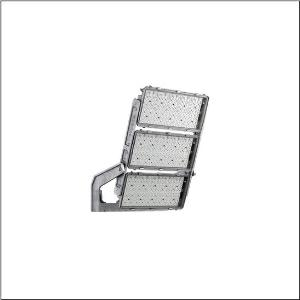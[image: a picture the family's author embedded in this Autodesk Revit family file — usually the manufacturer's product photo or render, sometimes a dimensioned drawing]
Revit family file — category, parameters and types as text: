
# Revit family: floodlight_fl_11_maxi_pro_remote___pl43_5xa779528a01aa_9860
name_source: partatom
category: Lighting Fixtures
units: mm (PartAtom-declared; Revit-internal decimal feet)

## family parameters
Cut with Voids When Loaded = No
Host = Face
Light Source = No
Part Type = Normal
Room Calculation Point = No
Round Connector Dimension = Use Diameter
Shared = No

## types (1)
- --- (1 x LED, 156040 lm, 1388 W, 5700K)
    Apparent Load = 1388 VA
    CIE Flux Codes = 25 74 99 100 100
    Color Rendering = 80
    Color Temperature = 5700K
    Default Elevation = 1800 mm
    Description = Floodlight FL 11  maxi  pro Remote floodlight; light control with lens of PMMA; cover panel of toughened safety glass, transparent; light distribution: PL43, asymmetric direct distribution, LEDcolour temperature: 5700K, rated luminous flux: 156.040lm, colour rendering: CRI > 80, light colour: 857; luminous efficacy: 112lm/W; brightness control: DMX+RDM; with terminal, 8-pole, max. 2.5mm², mains connection: 220..240V/380..400V AC, 50/60Hz, surge voltage resistance: line to ground: 10kV, ECG replaceable separately, LED unit replaceable without ESD environment, dustproof LED module, LED unit replaceable, LED unit replaceable on mast without ESD environment, dimming range 10..100%; 1388W floodlight with 3x LED unit of diecast aluminium, coated grey; length: 1.003mm / width: 651mm / height: 338mm; mounting bracket, of diecast aluminium, uncoated, natural, equipment: Power, protection rating (complete): IP66; insulation class (complete): insulation class I (protective earthing); certification: CE, ENEC, VDE; ball protection: ball impact resistance with accessories, impact resistance: IK07; only for outdoor installations, rated ambient temperature 10°C, permissible operating ambient temperature: -40..+30°C, permissible storage temperature: -40..+85°C; packaging unit: 1 piece

Light Distribution: PL43
    Height = 320 mm
    Lamp = 1 x LED
    Lamp Light Flux = 156040 lm
    Lamp Power = 1388 W
    Lamp count = 1
    Length = 1002 mm
    Luminous efficacy = 112 lm/W
    Manufacturer = Siteco
    ModVariant = No
    Model = 5XA779528A01AA
    Mounting Place = Ceiling
    Mounting Type = Surface mounted
    Number of Poles = 1
    OnlyDefault = Yes
    Power Factor = 1
    Product Name = Floodlight FL 11 maxi pro Remote | PL43
    Product group = floodlight | ceiling mounted
    ProductGroupID = 302
    Protection Class = Protection class I
    Protection Degree = IP 66
    RLX_Detail_Level = 1
    RLX_Emergency_Light_Flux = 0 lm
    RLX_Emergency_Type = 0
    RLX_Emergency_Type_DB = No
    RlxData = <blob elided: 52373 chars, md5=cbcdc4d1>
    Socket = socket
    Standby Power = 0 W
    System Light Flux = 156040 lm
    System Power = 1388 W
    Type Comments = factory setting: luminous flux: 100 % | dim-lin: 255 | 955 mA
    Type Image = l_1006784.jpg
    URL = http://relux.com
    VarID = @adj_014703
    Voltage = 0 V
    Weight = 0.00 kg
    Width = 655 mm

## geometry (parser evidence)
native form markers: Blend x4, Sweep x12
no freeform markers — native parametric forms only
